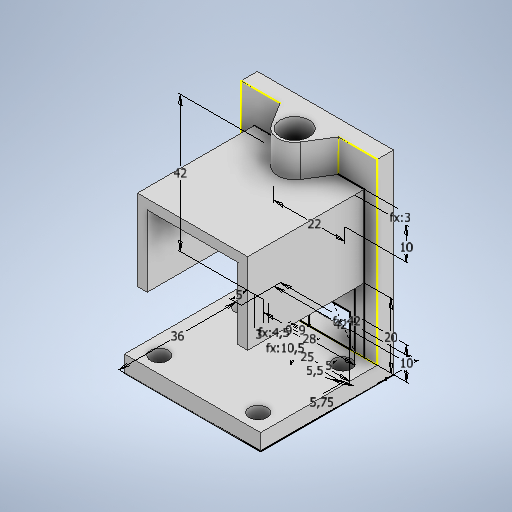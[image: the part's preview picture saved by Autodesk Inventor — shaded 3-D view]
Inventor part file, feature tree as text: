
AUTODESK INVENTOR PART (.ipt)
format: ipt  version: 2025 (Build 290162000, 162)  size: 348,160 bytes
history: native  units: mm
features: extrude x8, sketch x2, other x1, projected_geometry x1
ambient origin geometry x8: Origin, YZ Plane, XZ Plane, XY Plane, X Axis, Y Axis, Z Axis, Center Point
bodies: Body1 (feature_tree)
feature tree (12):
  other  "Bryła1"
  sketch  "Szkic1"
  extrude  "Wyciągnięcie proste1"  Depth=5.5mm
  extrude  "Wyciągnięcie proste2"  Depth=5.75mm
  extrude  "Wyciągnięcie proste3"  Depth=5.0mm
  extrude  "Wyciągnięcie proste4"  Depth=5.0mm
  sketch  "Szkic3"
  extrude  "Wyciągnięcie proste5"  Depth=42.0mm
  extrude  "Wyciągnięcie proste6"  Depth=4.5mm
  extrude  "Wyciągnięcie proste7"  Depth=10.5mm
  extrude  "Wyciągnięcie proste8"  Depth=9.0mm
  projected_geometry  "Pętla rzutowana1"
